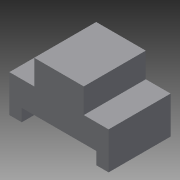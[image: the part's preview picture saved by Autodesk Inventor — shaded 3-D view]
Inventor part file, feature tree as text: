
AUTODESK INVENTOR PART (.ipt)
format: ipt  version: 2015 (Build 190159000, 159)  size: 83,456 bytes
history: native  units: in
note: dims shown in document units (in); Inventor stores cm internally (conversion verified against a paired STEP export)
features: extrude x1, sketch x1
ambient origin geometry x8: Origin, YZ Plane, XZ Plane, XY Plane, X Axis, Y Axis, Z Axis, Center Point
bodies: Solid1 (feature_tree)
feature tree (2):
  extrude  "Extrusion1"  Depth=0.25in
  sketch  "Sketch1"  dims[d0=0.75in d1=0.25in d2=0.25in d3=0.25in d4=0.25in d5=0.5in d6=0.5in d7=1.0in d8=0.5in d9=1.25in d10=0.0in]
